# Revit family: 601-A-005-DN40-50
name_source: partatom
category: Pipe Accessories
units: mm (PartAtom-declared; Revit-internal decimal feet)

## family parameters
Always vertical = Yes
Cut with Voids When Loaded = No
Part Type = Valve - Breaks Into
Round Connector Dimension = Use Diameter
Shared = No
Work Plane-Based = No

## types (2) — shared parameters
DN40_46-63 = 601-063-000-4100
DN50_57-74 = 601-074-000-4100
Description_ = AVK UNIVERSAL SUPA® STRAIGHT COUPLING
L = 190 mm
L1 = 100 mm  [stored 0.328084 ft]
PCD = 137 mm  [stored 0.449475 ft]
URL_product_pages = https://www.avkvalves.com

## per-type parameters (varying)
| type | DN | DN2 | DN_Ref | Side_length |
| DN40_46-63 | 40 mm  [stored 0.131234 ft] | 32 mm  [stored 0.104987 ft] | 64 mm  [stored 0.209974 ft] | 163 mm  [stored 0.534777 ft] |
| DN50_57-74 | 50 mm  [stored 0.164042 ft] | 37 mm  [stored 0.121391 ft] | 74 mm  [stored 0.242782 ft] | 174 mm  [stored 0.570866 ft] |

note: [stored X ft] marks values corroborated as IEEE doubles in the binary element streams (Revit-internal decimal feet)

## geometry (parser evidence)
native form markers: Sweep x4
no freeform markers — native parametric forms only
